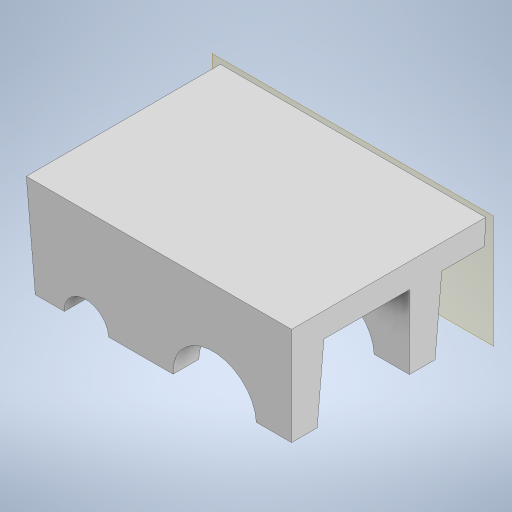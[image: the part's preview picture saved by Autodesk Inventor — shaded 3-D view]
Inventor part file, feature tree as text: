
AUTODESK INVENTOR PART (.ipt)
format: ipt  version: 2023 (Build 270158000, 158)  size: 294,400 bytes
history: native  units: in
note: dims shown in document units (in); Inventor stores cm internally (conversion verified against a paired STEP export)
features: extrude x3, sketch x2, plane x1, draft x1
ambient origin geometry x8: Origin, YZ Plane, XZ Plane, XY Plane, X Axis, Y Axis, Z Axis, Center Point
bodies: Solid1 (feature_tree)
feature tree (7):
  extrude  "Extrusion1"  Depth=5.0in
  extrude  "Extrusion2"  Depth=0.5in
  plane  "Work Plane1"
  sketch  "Sketch5"  dims[d3=7.4in d4=0.0in d15=1.4in d16=3.7in d17=6.0in d18=0.5in d20=2.528in d21=7.4in d22=0.0in d25=1.5in d26=0.866in d31=1.2546in d32=0.5669in d33=2.0in d34=1.5in d35=0.0172in d36=9.0in d37=0.0in d27=0.5in d28=0.0344in d29=0.0in d30=0.0in d38=0.5in d39=0.0344in]
  draft  "FaceDraft1"
  extrude  "Extrusion5"  Depth=0.5in
  sketch  "Sketch1"  dims[d0=5.0in d2=1.625in]
